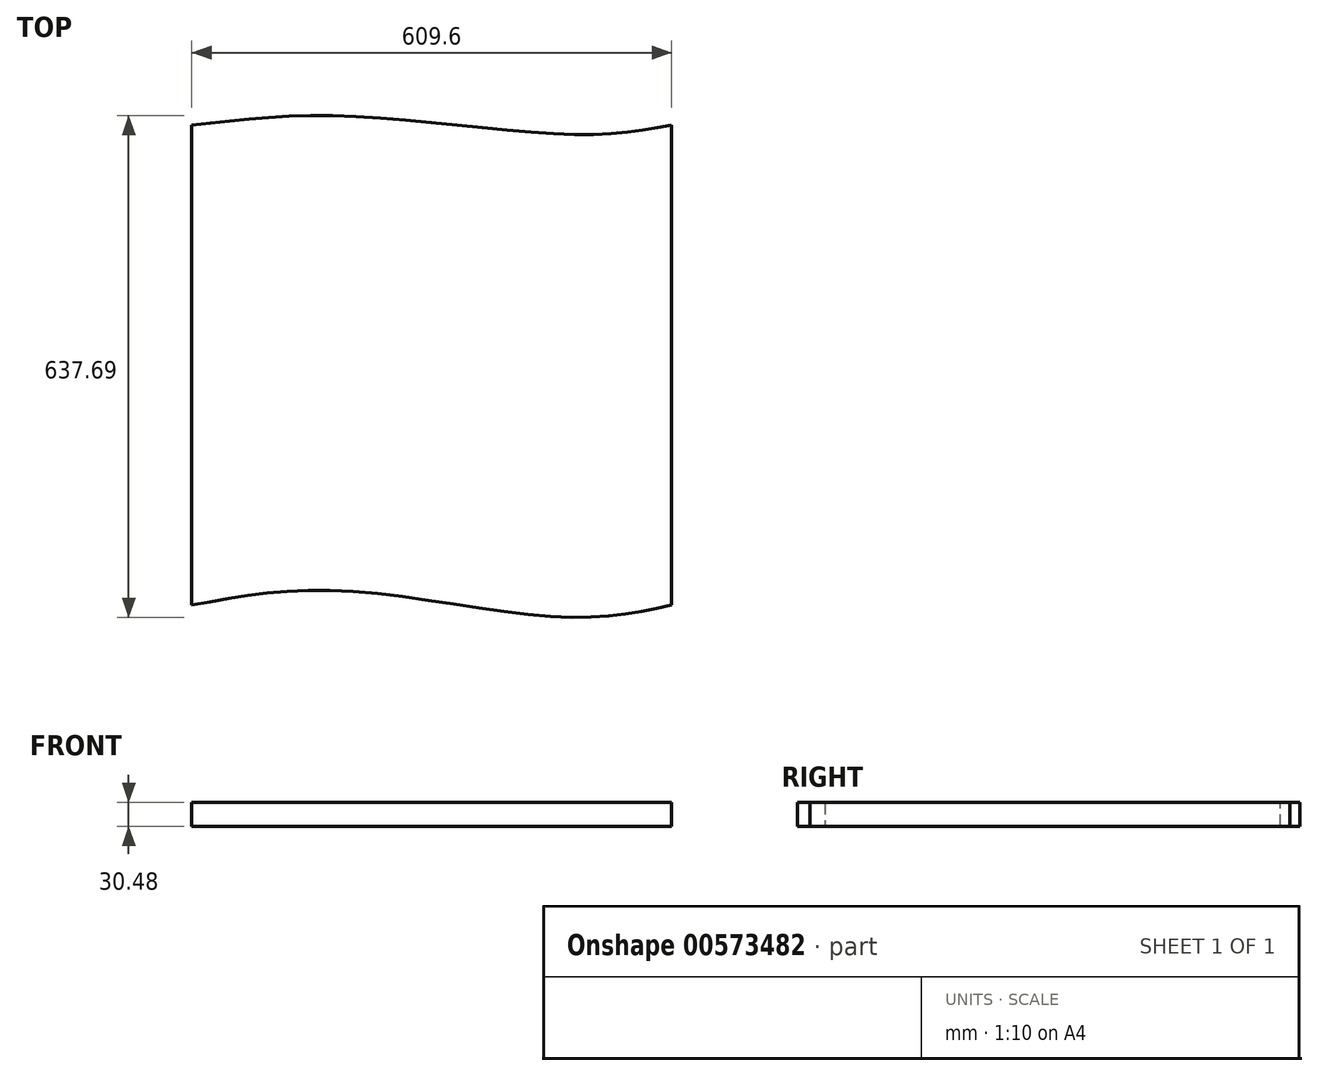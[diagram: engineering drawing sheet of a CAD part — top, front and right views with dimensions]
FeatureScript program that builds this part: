
annotation { "Feature Type Name" : "Feature", "Feature Type Description" : "" }
export const myFeature = defineFeature(function(context is Context, id is Id, definition is map)
    precondition{}
    {
        {
            var Q0;
            Q0=qCreatedBy(makeId("Top.planeOp"),FACE);
            var sketch = newSketch(context, id + "F0", { "sketchPlane" : qUnion([Q0])});
            skLineSegment(sketch, "E0.left", {"start": v(0, 0) * mm, "end": v(0, 609.6) * mm});
            skLineSegment(sketch, "E0.right", {"start": v(609.6, 0) * mm, "end": v(609.6, 609.6) * mm});
            skFitSpline(sketch, "E1", {"points": [v(0, 609.6) * mm, v(198.84, 621.37) * mm, v(482.71, 597.9) * mm, v(609.6, 609.6) * mm], "startDerivative": vector(549.5, 66.22) * mm, "endDerivative": vector(416.9, 71.82) * mm});
            skFitSpline(sketch, "E2", {"points": [v(0, 0) * mm, v(189.83, 18.3) * mm, v(473.15, -15.28) * mm, v(609.6, 0) * mm], "startDerivative": vector(535.93, 100.72) * mm, "endDerivative": vector(437.6, 95.08) * mm});
            skSolve(sketch);
        }
        {
            var Q0;
            Q0=makeQuery(id+"F0.imprint","IMPRINT",FACE,{"disambiguationData":[TD([[makeQuery(id+"F0.imprint","IMPRINT",EDGE,{"derivedFrom":sQuery(id+"F0.wireOp",EDGE,"E0.left")}),-1.0]])]});
            extrude(context, id + "F1", {"entities" : qUnion([Q0]), "depth" : 30.48 * mm, "offsetDistance" : 25.4 * mm});
        }
    });
